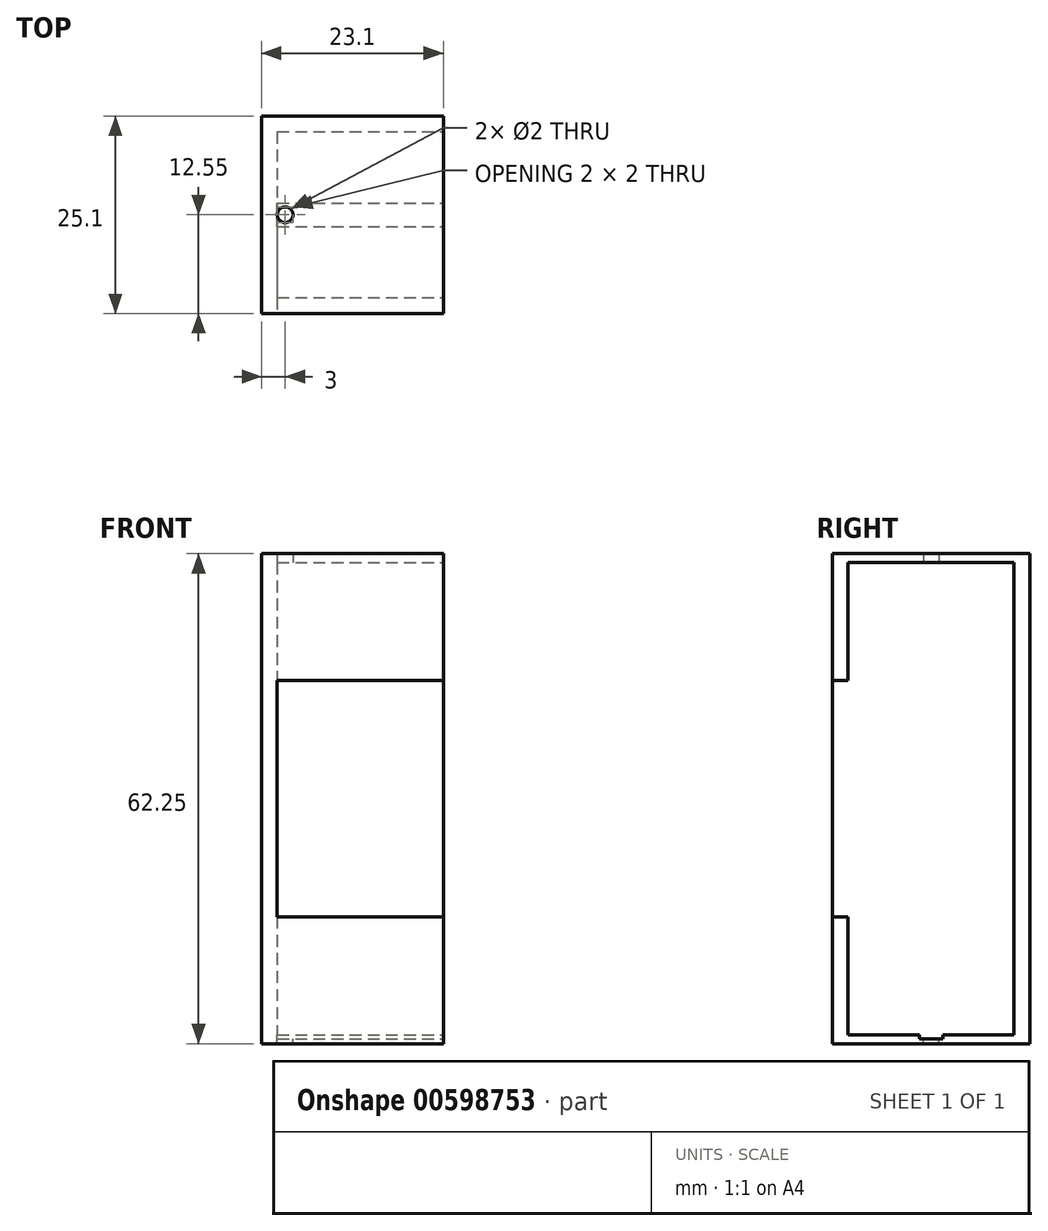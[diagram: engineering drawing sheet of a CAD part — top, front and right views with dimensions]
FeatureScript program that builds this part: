
annotation { "Feature Type Name" : "Feature", "Feature Type Description" : "" }
export const myFeature = defineFeature(function(context is Context, id is Id, definition is map)
    precondition{}
    {
        {
            var Q0;
            Q0=qCreatedBy(makeId("Top.planeOp"),FACE);
            var sketch = newSketch(context, id + "F0", { "sketchPlane" : qUnion([Q0])});
            skLineSegment(sketch, "E0.bottom", {"start": v(11.55, 12.55) * mm, "end": v(-11.55, 12.55) * mm});
            skLineSegment(sketch, "E0.top", {"start": v(11.55, -12.55) * mm, "end": v(-11.55, -12.55) * mm});
            skLineSegment(sketch, "E0.left", {"start": v(11.55, 12.55) * mm, "end": v(11.55, -12.55) * mm});
            skLineSegment(sketch, "E0.right", {"start": v(-11.55, 12.55) * mm, "end": v(-11.55, -12.55) * mm});
            skPoint(sketch, "E0.middle", {"position": v(0, 0) * mm});
            skSolve(sketch);
        }
        {
            var Q0;
            Q0=makeQuery(id+"F0.imprint","IMPRINT",FACE,{"disambiguationData":[TD([[makeQuery(id+"F0.imprint","IMPRINT",EDGE,{"derivedFrom":sQuery(id+"F0.wireOp",EDGE,"E0.bottom")}),1.0]])]});
            extrude(context, id + "F1", {"entities" : qUnion([Q0]), "depth" : 62.25 * mm, "offsetDistance" : 25 * mm});
        }
        {
            var Q0;
            Q0=makeQuery(id+"F1.opExtrude","SWEPT_FACE",FACE,{"disambiguationData":[OSD([sQuery(id+"F0.wireOp",EDGE,"E0.left")])]});
            var sketch = newSketch(context, id + "F2", { "sketchPlane" : qUnion([Q0])});
            skLineSegment(sketch, "E1.bottom", {"start": v(10.55, 61.12) * mm, "end": v(-10.55, 61.12) * mm});
            skLineSegment(sketch, "E1.top", {"start": v(10.55, 1.13) * mm, "end": v(-10.55, 1.12) * mm});
            skLineSegment(sketch, "E1.left", {"start": v(10.55, 61.12) * mm, "end": v(10.55, 1.13) * mm});
            skLineSegment(sketch, "E1.right", {"start": v(-10.55, 61.12) * mm, "end": v(-10.55, 1.13) * mm});
            skPoint(sketch, "E1.middle", {"position": v(0, 31.12) * mm});
            skPoint(sketch, "E1.middle.positionSnap0", {"position": v(-12.55, 31.12) * mm});
            skPoint(sketch, "E1.centerSnap0", {"position": v(-12.55, 31.12) * mm});
            skSolve(sketch);
        }
        {
            var Q0;
            Q0=makeQuery(id+"F2.imprint","IMPRINT",FACE,{"disambiguationData":[TD([[makeQuery(id+"F2.imprint","IMPRINT",EDGE,{"derivedFrom":sQuery(id+"F2.wireOp",EDGE,"E1.bottom")}),1.0]])]});
            extrude(context, id + "F3", {"entities" : qUnion([Q0]), "operationType" : NewBodyOperationType.REMOVE, "oppositeDirection" : true, "depth" : 21.1 * mm, "offsetDistance" : 25 * mm});
        }
        {
            var Q0;
            Q0=makeQuery(id+"F1.opExtrude","SWEPT_FACE",FACE,{"disambiguationData":[OSD([sQuery(id+"F0.wireOp",EDGE,"E0.left")])]});
            var sketch = newSketch(context, id + "F4", { "sketchPlane" : qUnion([Q0])});
            skLineSegment(sketch, "E2.bottom", {"start": v(-1.5, 0.62) * mm, "end": v(1.5, 0.62) * mm});
            skLineSegment(sketch, "E2.top", {"start": v(-1.5, 1.62) * mm, "end": v(1.5, 1.62) * mm});
            skLineSegment(sketch, "E2.left", {"start": v(-1.5, 0.62) * mm, "end": v(-1.5, 1.62) * mm});
            skLineSegment(sketch, "E2.right", {"start": v(1.5, 0.62) * mm, "end": v(1.5, 1.62) * mm});
            skPoint(sketch, "E2.middle", {"position": v(0, 1.12) * mm});
            skSolve(sketch);
        }
        {
            var Q0;
            {var subQ0=sQuery(id+"F4.wireOp",EDGE,"E2.bottom");Q0=makeQuery(id+"F4.imprint","IMPRINT",FACE,{"disambiguationData":[TD([[makeQuery(id+"F4.imprint","IMPRINT",EDGE,{"derivedFrom":subQ0}),1.0]])]});}
            extrude(context, id + "F5", {"entities" : qUnion([Q0]), "operationType" : NewBodyOperationType.REMOVE, "oppositeDirection" : true, "depth" : 21.1 * mm, "offsetDistance" : 25 * mm});
        }
        {
            var Q0;
            Q0=makeQuery(id+"F1.opExtrude","SWEPT_FACE",FACE,{"disambiguationData":[OSD([sQuery(id+"F0.wireOp",EDGE,"E0.left")])]});
            var sketch = newSketch(context, id + "F6", { "sketchPlane" : qUnion([Q0])});
            skLineSegment(sketch, "E3.bottom", {"start": v(12.55, 46.12) * mm, "end": v(8.55, 46.12) * mm});
            skLineSegment(sketch, "E3.top", {"start": v(12.55, 16.12) * mm, "end": v(8.55, 16.12) * mm});
            skLineSegment(sketch, "E3.left", {"start": v(12.55, 46.12) * mm, "end": v(12.55, 16.12) * mm});
            skLineSegment(sketch, "E3.right", {"start": v(8.55, 46.12) * mm, "end": v(8.55, 16.12) * mm});
            skPoint(sketch, "E3.middle", {"position": v(10.55, 31.12) * mm});
            skLineSegment(sketch, "E4.bottom", {"start": v(-10.55, 46.12) * mm, "end": v(-14.55, 46.12) * mm});
            skLineSegment(sketch, "E4.top", {"start": v(-10.55, 16.13) * mm, "end": v(-14.55, 16.13) * mm});
            skLineSegment(sketch, "E4.left", {"start": v(-10.55, 46.12) * mm, "end": v(-10.55, 16.12) * mm});
            skLineSegment(sketch, "E4.right", {"start": v(-14.55, 46.12) * mm, "end": v(-14.55, 16.12) * mm});
            skPoint(sketch, "E4.middle", {"position": v(-12.55, 31.12) * mm});
            skSolve(sketch);
        }
        {
            var Q0;
            {var subQ0=sQuery(id+"F6.wireOp",EDGE,"E4.left");Q0=makeQuery(id+"F6.imprint","IMPRINT",FACE,{"disambiguationData":[TD([[makeQuery(id+"F6.imprint","IMPRINT",EDGE,{"derivedFrom":subQ0}),-1.0]])]});}
            extrude(context, id + "F7", {"entities" : qUnion([Q0]), "operationType" : NewBodyOperationType.REMOVE, "oppositeDirection" : true, "depth" : 21.1 * mm, "offsetDistance" : 25 * mm});
        }
        {
            var Q0;
            Q0=makeQuery(id+"F3.boolean.opBoolean","COPY",FACE,{"derivedFrom":makeQuery(id+"F3.opExtrude","SWEPT_FACE",FACE,{"disambiguationData":[OSD([sQuery(id+"F2.wireOp",EDGE,"E1.bottom")])]})});
            var sketch = newSketch(context, id + "F8", { "sketchPlane" : qUnion([Q0])});
            skLineSegment(sketch, "E5", {"start": v(-9.55, 0) * mm, "end": v(-8.55, 0) * mm});
            skSolve(sketch);
        }
        {
            var Q0;
            Q0=sQuery(id+"F8.wireOp",VERTEX,"E5.end");
            var Q1;
            Q1=makeQuery(id+"F1.opExtrude","SWEPT_BODY",BODY,{"disambiguationData":[OSD([sQuery(id+"F0.wireOp",EDGE,"E0.bottom"),sQuery(id+"F0.wireOp",EDGE,"E0.top"),sQuery(id+"F0.wireOp",EDGE,"E0.left"),sQuery(id+"F0.wireOp",EDGE,"E0.right")])]});
            hole(context, id + "F9", {"style" : HoleStyle.SIMPLE, "endStyle" : HoleEndStyle.BLIND, "holeDiameter" : 2 * mm, "majorDiameter" : 5 * mm, "holeDepth" : 2 * mm, "isTappedThrough" : true, "tappedDepth" : 12 * mm, "tapClearance" : 3, "locations" : qUnion([Q0]), "scope" : qUnion([Q1])});
        }
        {
            var Q0;
            Q0=makeQuery(id+"F5.boolean.opBoolean","COPY",FACE,{"derivedFrom":makeQuery(id+"F5.opExtrude","SWEPT_FACE",FACE,{"disambiguationData":[OSD([sQuery(id+"F4.wireOp",EDGE,"E2.bottom")])]})});
            var sketch = newSketch(context, id + "F10", { "sketchPlane" : qUnion([Q0])});
            skLineSegment(sketch, "E6", {"start": v(-9.55, 0) * mm, "end": v(-8.55, 0) * mm});
            skSolve(sketch);
        }
        {
            var Q0;
            Q0=sQuery(id+"F10.wireOp",VERTEX,"E6.end");
            var Q1;
            Q1=makeQuery(id+"F1.opExtrude","SWEPT_BODY",BODY,{"disambiguationData":[OSD([sQuery(id+"F0.wireOp",EDGE,"E0.bottom"),sQuery(id+"F0.wireOp",EDGE,"E0.top"),sQuery(id+"F0.wireOp",EDGE,"E0.left"),sQuery(id+"F0.wireOp",EDGE,"E0.right")])]});
            hole(context, id + "F11", {"style" : HoleStyle.SIMPLE, "endStyle" : HoleEndStyle.BLIND, "holeDiameter" : 2 * mm, "majorDiameter" : 5 * mm, "holeDepth" : 2 * mm, "isTappedThrough" : true, "tappedDepth" : 12 * mm, "tapClearance" : 3, "locations" : qUnion([Q0]), "scope" : qUnion([Q1])});
        }
    });
